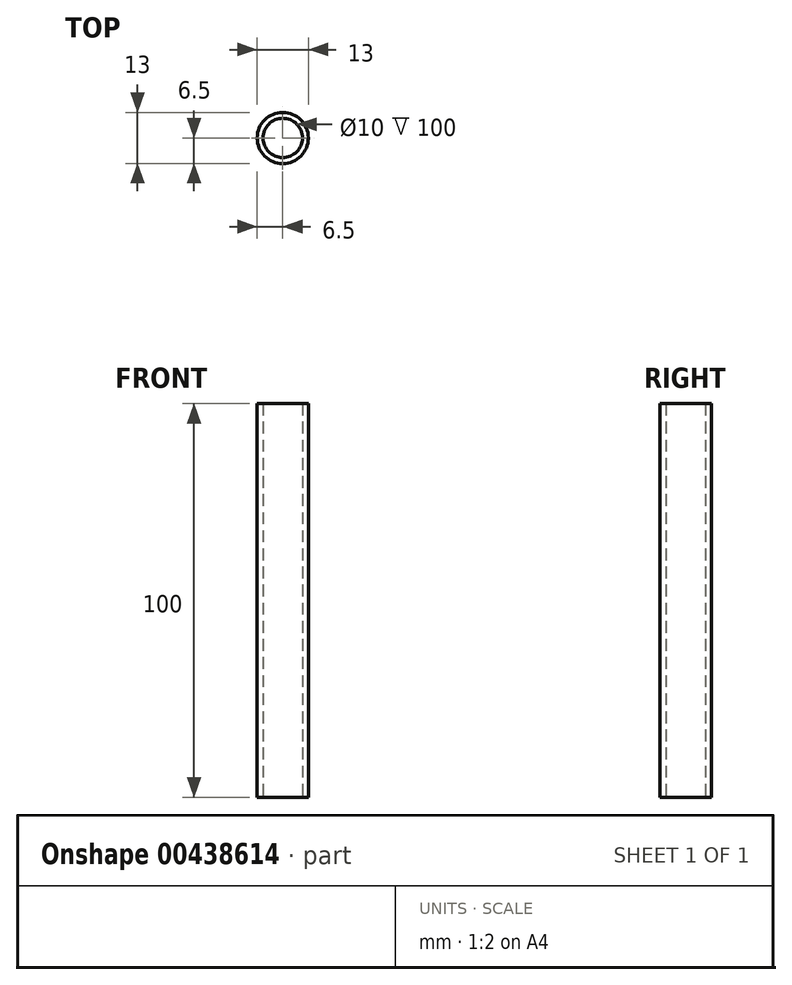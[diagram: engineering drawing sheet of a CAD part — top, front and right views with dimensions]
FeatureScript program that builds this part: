
annotation { "Feature Type Name" : "Feature", "Feature Type Description" : "" }
export const myFeature = defineFeature(function(context is Context, id is Id, definition is map)
    precondition{}
    {
        {
            var Q0;
            Q0=qCreatedBy(makeId("Top.planeOp"),FACE);
            var sketch = newSketch(context, id + "F0", { "sketchPlane" : qUnion([Q0])});
            skCircle(sketch, "E0", {"center": v(0, 0) * mm, "radius": 6.5 * mm});
            skCircle(sketch, "E1", {"center": v(0, 0) * mm, "radius": 5 * mm});
            skSolve(sketch);
        }
        {
            var Q0;
            Q0 = qSketchRegion(id + "F0", true);
            extrude(context, id + "F1", {"entities" : qUnion([Q0]), "depth" : 100 * mm});
        }
    });
